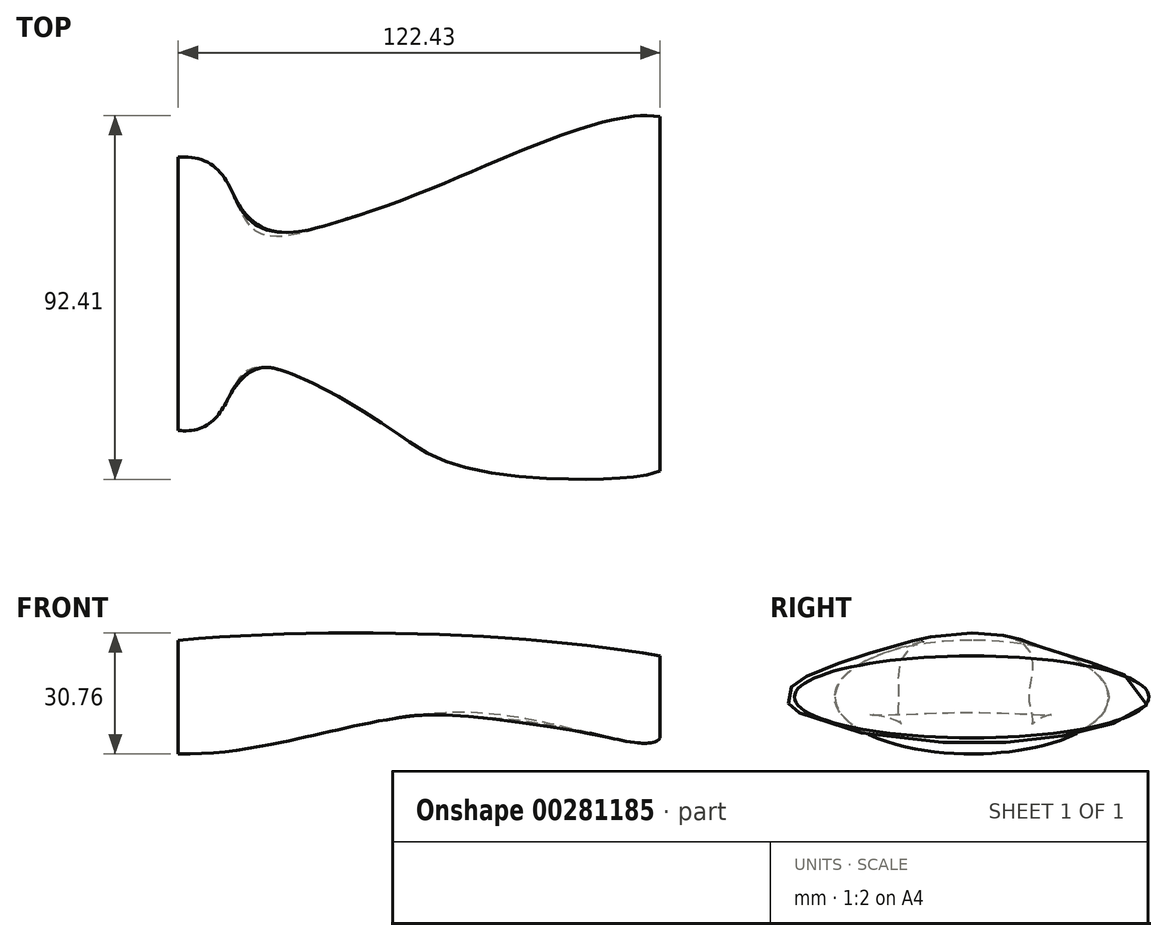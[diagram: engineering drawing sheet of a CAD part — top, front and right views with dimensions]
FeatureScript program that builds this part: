
annotation { "Feature Type Name" : "Feature", "Feature Type Description" : "" }
export const myFeature = defineFeature(function(context is Context, id is Id, definition is map)
    precondition{}
    {
        {
            var Q0;
            Q0=qCreatedBy(makeId("Right.planeOp"),FACE);
            cPlane(context, id + "F0", {"entities" : qUnion([Q0]), "cplaneType" : CPlaneType.OFFSET, "offset" : 122.43 * mm, "width" : 152.4 * mm, "height" : 152.4 * mm});
        }
        {
            var Q0;
            Q0=qCreatedBy(makeId("Right.planeOp"),FACE);
            var sketch = newSketch(context, id + "F1", { "sketchPlane" : qUnion([Q0])});
            skEllipse(sketch, "E0", {"center": v(0, 0) * mm, "majorRadius": 34.74 * mm, "minorRadius": 14.43 * mm, "majorAxis": v(-1, 0)});
            skSolve(sketch);
        }
        {
            var Q0;
            Q0=qCreatedBy(id+"F0.planeOp",FACE);
            var sketch = newSketch(context, id + "F2", { "sketchPlane" : qUnion([Q0])});
            skEllipse(sketch, "E1", {"center": v(0, 0) * mm, "majorRadius": 45.04 * mm, "minorRadius": 10.4 * mm, "majorAxis": v(-1, 0)});
            skSolve(sketch);
        }
        {
            var Q0;
            Q0=qCreatedBy(makeId("Front.planeOp"),FACE);
            var sketch = newSketch(context, id + "F3", { "sketchPlane" : qUnion([Q0])});
            skFitSpline(sketch, "E2", {"points": [v(0, 14.43) * mm, v(122.43, 10.4) * mm], "startDerivative": vector(117.9, 10.78) * mm, "endDerivative": vector(98.71, -17.78) * mm});
            skFitSpline(sketch, "E3", {"points": [v(0, -14.43) * mm, v(76.9, -4.1) * mm, v(122.43, -10.4) * mm], "startDerivative": vector(136.1, -3.85) * mm, "endDerivative": vector(21, 34.07) * mm});
            skSolve(sketch);
        }
        {
            var Q0;
            Q0=qCreatedBy(makeId("Top.planeOp"),FACE);
            var sketch = newSketch(context, id + "F4", { "sketchPlane" : qUnion([Q0])});
            skFitSpline(sketch, "E4", {"points": [v(0, -34.74) * mm, v(16.1, -20.69) * mm, v(29.6, -20.66) * mm, v(54.02, -34.4) * mm, v(74.87, -44.64) * mm, v(122.43, -45.04) * mm], "startDerivative": vector(188.2, -18.9) * mm, "endDerivative": vector(77.61, 32.7) * mm});
            skFitSpline(sketch, "E5", {"points": [v(0, 34.74) * mm, v(18.47, 16.94) * mm, v(37.9, 17.45) * mm, v(61.69, 25.7) * mm, v(103.28, 42.3) * mm, v(122.43, 45.04) * mm], "startDerivative": vector(210.26, 14.83) * mm, "endDerivative": vector(83.38, -12.16) * mm});
            skSolve(sketch);
        }
        {
            var Q0;
            Q0=makeQuery(id+"F1.imprint","IMPRINT",FACE,{"disambiguationData":[TD([[makeQuery(id+"F1.imprint","IMPRINT",EDGE,{"derivedFrom":sQuery(id+"F1.wireOp",EDGE,"E0")}),1.0]])]});
            var Q1;
            Q1=makeQuery(id+"F2.imprint","IMPRINT",FACE,{"disambiguationData":[TD([[makeQuery(id+"F2.imprint","IMPRINT",EDGE,{"derivedFrom":sQuery(id+"F2.wireOp",EDGE,"E1")}),1.0]])]});
            var Q2;
            Q2=sQuery(id+"F4.wireOp",EDGE,"E4");
            var Q3;
            Q3=sQuery(id+"F4.wireOp",EDGE,"E5");
            var Q4;
            Q4=sQuery(id+"F3.wireOp",EDGE,"E2");
            var Q5;
            Q5=sQuery(id+"F3.wireOp",EDGE,"E3");
            loft(context, id + "F5", {"addGuides" : true, "sheetProfilesArray" : [{ "sheetProfileEntities" : qUnion([Q0]) }, { "sheetProfileEntities" : qUnion([Q1]) }], "guidesArray" : [{ "guideEntities" : qUnion([Q2]), "guideDerivativeType" : LoftGuideDerivativeType.DEFAULT, "guideDerivativeMagnitude" : 1 }, { "guideEntities" : qUnion([Q3]), "guideDerivativeType" : LoftGuideDerivativeType.DEFAULT, "guideDerivativeMagnitude" : 1 }, { "guideEntities" : qUnion([Q4]), "guideDerivativeType" : LoftGuideDerivativeType.DEFAULT, "guideDerivativeMagnitude" : 1 }, { "guideEntities" : qUnion([Q5]), "guideDerivativeType" : LoftGuideDerivativeType.DEFAULT, "guideDerivativeMagnitude" : 1 }]});
        }
    });
